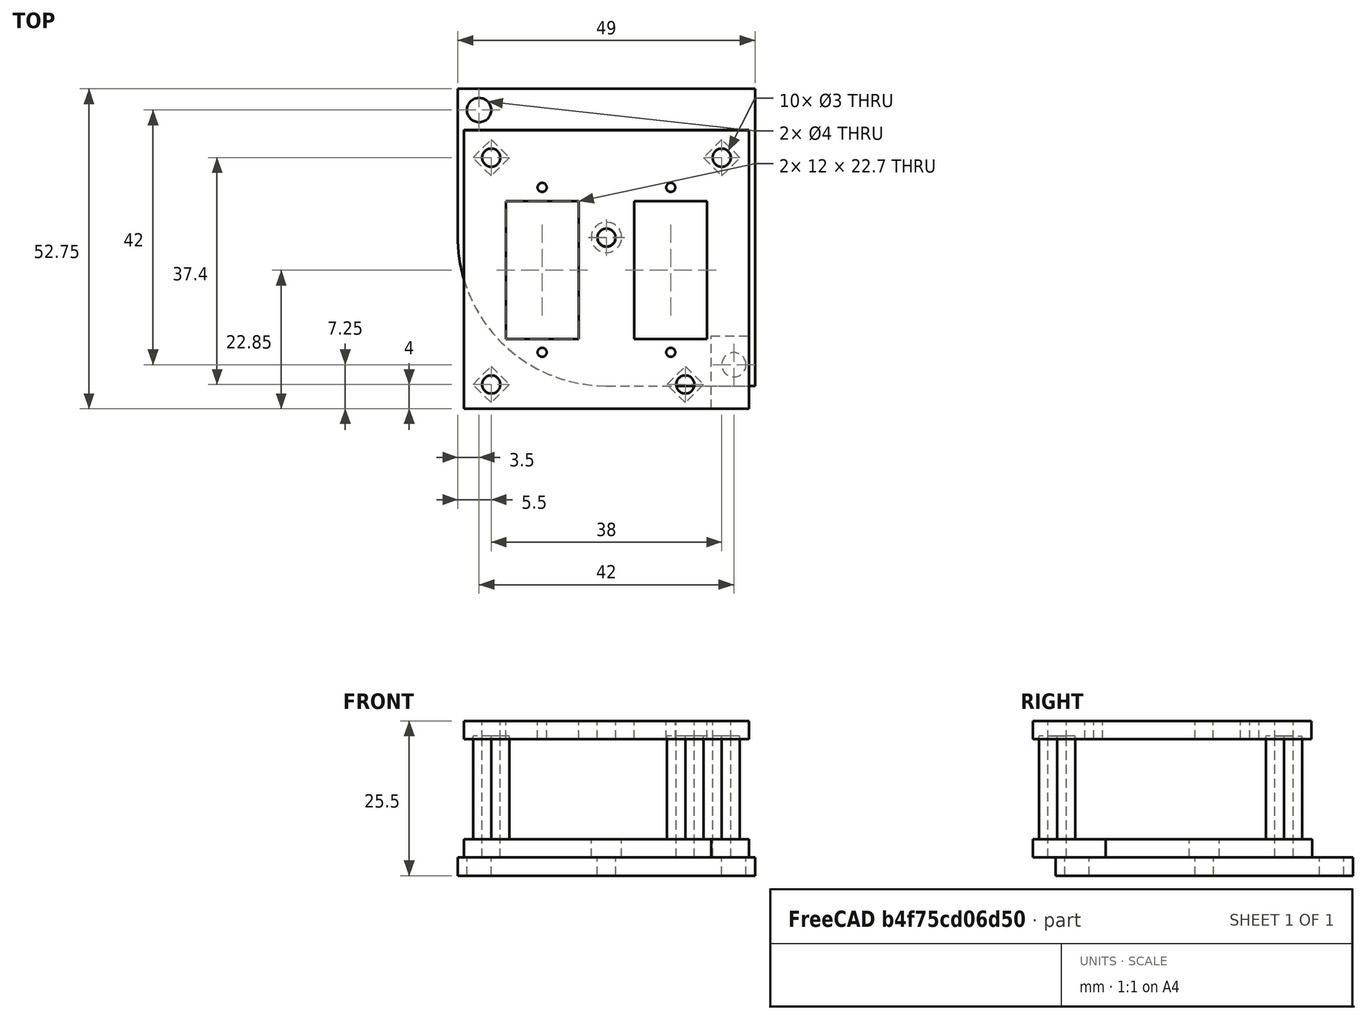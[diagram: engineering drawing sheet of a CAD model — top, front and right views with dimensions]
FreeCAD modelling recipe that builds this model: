
FCSTD DOCUMENT  (FreeCAD 0.17R13541 (Git))
Label: Temp gauge
License: All rights reserved
LicenseURL: http://en.wikipedia.org/wiki/All_rights_reserved
objects: Part::Cylinder×14, Part::Cut×13, Part::Box×7, Part::FeaturePython×5, Part::MultiFuse×4, Part::Prism×3, Part::Fuse×2
note: 48 computed .brp shape members not serialized (recipe doc carries the construction recipe); baked Part::Feature solids carry a one-line shape summary decoded from their .brp

FEATURE [Part::Box] Box  label="Temp plate"
  AttacherType = Attacher::AttachEngine3D
  Height = 3
  Length = 49
  Width = 49
FEATURE [Part::Box] Box001  label="Recorte"
  AttacherType = Attacher::AttachEngine3D
  Height = 3
  Length = 24.5
  Width = 24.5
FEATURE [Part::Cut] Cut
  Base = -> Box
  Refine = true
  Tool = -> Box001
FEATURE [Part::Cylinder] Cylinder  label="Cilindro"
  Angle = 360
  AttacherType = Attacher::AttachEngine3D
  Height = 3
  Placement = pos=(24.5,24.5,0) rot=(0,0,1;0rad)
  Radius = 24.5
FEATURE [Part::MultiFuse] Fusion  label="Temp plate recortada"
  Refine = true
  Shapes = -> [Cut,Cylinder]
FEATURE [Part::Cylinder] Cylinder001  label="Taladro 1"
  Angle = 360
  AttacherType = Attacher::AttachEngine3D
  Height = 10
  Placement = pos=(3.5,45.5,0) rot=(0,0,1;0rad)
  Radius = 2
FEATURE [Part::Cylinder] Cylinder002  label="Taladro 2"
  Angle = 360
  AttacherType = Attacher::AttachEngine3D
  Height = 10
  Placement = pos=(45.5,3.5,0) rot=(0,0,1;0rad)
  Radius = 2
FEATURE [Part::Cylinder] Cylinder003  label="Taladro 3"
  Angle = 360
  AttacherType = Attacher::AttachEngine3D
  Height = 10
  Placement = pos=(24.5,24.5,0) rot=(0,0,1;0rad)
  Radius = 1.5
FEATURE [Part::Cut] Cut001
  Base = -> Fusion
  Refine = true
  Tool = -> Cylinder001
FEATURE [Part::Cut] Cut002
  Base = -> Cut001
  Refine = true
  Tool = -> Cylinder002
FEATURE [Part::Cut] Cut003  label="temp plate final"
  Base = -> Cut002
  Refine = true
  Tool = -> Cylinder003
FEATURE [Part::Box] Box002  label="top plate 2"
  AttacherType = Attacher::AttachEngine3D
  Height = 3
  Length = 47
  Placement = pos=(3.25,-1.5,3) rot=(0,0,1;0rad)
  Width = 46
FEATURE [Part::Cylinder] Cylinder004  label="taladro 3"
  Angle = 360
  AttacherType = Attacher::AttachEngine3D
  Height = 10
  Placement = pos=(26.75,26.75,0) rot=(0,0,1;0rad)
  Radius = 2.5
FEATURE [Part::Cylinder] Cylinder005  label="taladro 4"
  Angle = 360
  AttacherType = Attacher::AttachEngine3D
  Height = 27
  Placement = pos=(7.75,2.5,0) rot=(0,0,1;0rad)
  Radius = 1.5
FEATURE [Part::Box] Box003  label="base 2"
  AttacherType = Attacher::AttachEngine3D
  Height = 3
  Length = 47
  Placement = pos=(3.25,-1.5,22.5) rot=(0,0,1;0rad)
  Width = 45.9
FEATURE [Part::Box] Box004  label="Taladro servomotor"
  AttacherType = Attacher::AttachEngine3D
  Height = 10
  Length = 12
  Placement = pos=(10.15,10,19.5) rot=(0,0,1;0rad)
  Width = 22.7
FEATURE [Part::Cylinder] Cylinder006  label="taladro 5"
  Angle = 360
  AttacherType = Attacher::AttachEngine3D
  Height = 10
  Placement = pos=(7.75,2.5,19.5) rot=(0,0,1;0rad)
  Radius = 1.5
FEATURE [Part::Cylinder] Cylinder007  label="Taladro 6"
  Angle = 360
  AttacherType = Attacher::AttachEngine3D
  Height = 10
  Placement = pos=(26.75,26.7,19.5) rot=(0,0,1;0rad)
  Radius = 1.5
FEATURE [Part::Cylinder] Cylinder008  label="Taladro 7"
  Angle = 360
  AttacherType = Attacher::AttachEngine3D
  Height = 10
  Placement = pos=(16.15,7.8,19.5) rot=(0,0,1;0rad)
  Radius = 0.75
FEATURE [Part::Cylinder] Cylinder009  label="taladro adicional 3"
  Angle = 360
  AttacherType = Attacher::AttachEngine3D
  Height = 27
  Placement = pos=(45.75,39.9,0) rot=(0,0,1;0rad)
  Radius = 1.5
FEATURE [Part::Box] Box005  label="Recorte placa"
  AttacherType = Attacher::AttachEngine3D
  Height = 3
  Length = 10
  Placement = pos=(44,-2,3) rot=(0,0,1;0rad)
  Width = 11
FEATURE [Part::FeaturePython] Array002  label="Array taladro 4"  # Draft array (typed FeaturePython)
  Angle = 360
  ArrayType = 0
  Axis = (0,0,1)
  Base = -> Cylinder005
  Center = (0,0,0)
  Fuse = false
  IntervalAxis = (0,0,0)
  IntervalX = (38,0,0)
  IntervalY = (0,37.4,0)
  IntervalZ = (0,0,0)
  NumberPolar = 1
  NumberX = 1
  NumberY = 2
  NumberZ = 1
FEATURE [Part::Fuse] Fusion002  label="Taladros 2"
  Base = -> Cylinder004
  Refine = true
  Tool = -> Array002
FEATURE [Part::Prism] Prism  label="Columna"
  AttacherType = Attacher::AttachEngine3D
  Circumradius = 3
  Height = 20
  Placement = pos=(7.75,2.5,3) rot=(0,0,1;0rad)
  Polygon = 4
FEATURE [Part::FeaturePython] Array003  label="Array columnas"  # Draft array (typed FeaturePython)
  Angle = 360
  ArrayType = 0
  Axis = (0,0,1)
  Base = -> Prism
  Center = (0,0,0)
  Fuse = false
  IntervalAxis = (0,0,0)
  IntervalX = (38,0,0)
  IntervalY = (0,37.4,0)
  IntervalZ = (0,0,0)
  NumberPolar = 1
  NumberX = 1
  NumberY = 2
  NumberZ = 1
FEATURE [Part::Fuse] Fusion001  label="top plate columnas"
  Base = -> Box002
  Refine = true
  Tool = -> Array003
FEATURE [Part::Cut] Cut004  label="Top plate"
  Base = -> Fusion001
  Refine = true
  Tool = -> Fusion002
FEATURE [Part::Prism] Prism001  label="Columna 3"
  AttacherType = Attacher::AttachEngine3D
  Circumradius = 3
  Height = 20
  Placement = pos=(45.75,39.9,3) rot=(0,0,1;0rad)
  Polygon = 4
FEATURE [Part::MultiFuse] Fusion004  label="placa con tres taladros"
  Refine = true
  Shapes = -> [Cut004,Prism001]
FEATURE [Part::Prism] Prism002  label="Columna 4"
  AttacherType = Attacher::AttachEngine3D
  Circumradius = 3
  Height = 20
  Placement = pos=(39.75,2.5,3) rot=(0,0,1;0rad)
  Polygon = 4
FEATURE [Part::FeaturePython] Array004  label="Array taladro servomotor"  # Draft array (typed FeaturePython)
  Angle = 360
  ArrayType = 0
  Axis = (0,0,1)
  Base = -> Box004
  Center = (0,0,0)
  Fuse = false
  IntervalAxis = (0,0,0)
  IntervalX = (21.2,0,0)
  IntervalY = (0,1,0)
  IntervalZ = (0,0,0)
  NumberPolar = 1
  NumberX = 2
  NumberY = 1
  NumberZ = 1
FEATURE [Part::FeaturePython] Array005  label="Array taladro 5"  # Draft array (typed FeaturePython)
  Angle = 360
  ArrayType = 0
  Axis = (0,0,1)
  Base = -> Cylinder006
  Center = (0,0,0)
  Fuse = false
  IntervalAxis = (0,0,0)
  IntervalX = (38,0,0)
  IntervalY = (0,37.4,0)
  IntervalZ = (0,0,0)
  NumberPolar = 1
  NumberX = 1
  NumberY = 2
  NumberZ = 1
FEATURE [Part::FeaturePython] Array006  label="Array taladros 7"  # Draft array (typed FeaturePython)
  Angle = 360
  ArrayType = 0
  Axis = (0,0,1)
  Base = -> Cylinder008
  Center = (0,0,0)
  Fuse = false
  IntervalAxis = (0,0,0)
  IntervalX = (21.2,0,0)
  IntervalY = (0,27.2,0)
  IntervalZ = (0,0,0)
  NumberPolar = 1
  NumberX = 2
  NumberY = 2
  NumberZ = 1
FEATURE [Part::MultiFuse] Fusion003  label="Taladros 3"
  Refine = true
  Shapes = -> [Cylinder007,Array006,Array004,Array005]
FEATURE [Part::Cut] Cut005  label="base previa"
  Base = -> Box003
  Refine = true
  Tool = -> Fusion003
FEATURE [Part::Cut] Cut006  label="Placa con tres columnas"
  Base = -> Fusion004
  Refine = true
  Tool = -> Cylinder009
FEATURE [Part::Cut] Cut007  label="Placa tres columnas y tornillo"
  Base = -> Cut006
  Refine = true
  Tool = -> Box005
FEATURE [Part::Cylinder] Cylinder010  label="taladro adicional 4"
  Angle = 360
  AttacherType = Attacher::AttachEngine3D
  Height = 27
  Placement = pos=(39.75,2.5,0) rot=(0,0,1;0rad)
  Radius = 1.5
FEATURE [Part::Cut] Cut008
  Base = -> Cut007
  Refine = true
  Tool = -> Cylinder010
FEATURE [Part::Cylinder] Cylinder011  label="taladro adicional 005"
  Angle = 360
  AttacherType = Attacher::AttachEngine3D
  Height = 27
  Placement = pos=(39.75,2.5,0) rot=(0,0,1;0rad)
  Radius = 1.5
FEATURE [Part::Cut] Cut009
  Base = -> Prism002
  Refine = true
  Tool = -> Cylinder011
FEATURE [Part::MultiFuse] Fusion005  label="top plate final"
  Placement = pos=(-2.25,-2.25,0) rot=(0,0,1;0rad)
  Refine = true
  Shapes = -> [Cut008,Cut009]
FEATURE [Part::Cylinder] Cylinder012  label="taladro 006"
  Angle = 360
  AttacherType = Attacher::AttachEngine3D
  Height = 10
  Placement = pos=(45.75,39.9,19.5) rot=(0,0,1;0rad)
  Radius = 1.5
FEATURE [Part::Cut] Cut010  label="base 3 taladros"
  Base = -> Cut005
  Refine = true
  Tool = -> Cylinder012
FEATURE [Part::Cylinder] Cylinder013  label="taladro 007"
  Angle = 360
  AttacherType = Attacher::AttachEngine3D
  Height = 10
  Placement = pos=(39.75,2.5,18.5) rot=(0,0,1;0rad)
  Radius = 1.5
FEATURE [Part::Cut] Cut011  label="base final"
  Base = -> Cut010
  Placement = pos=(-2.25,-2.25,0) rot=(0,0,1;0rad)
  Refine = true
  Tool = -> Cylinder013
FEATURE [Part::Box] Box006  label="Recorte adicional"
  AttacherType = Attacher::AttachEngine3D
  Height = 3
  Length = 7.25
  Placement = pos=(41.75,0,3) rot=(0,0,1;0rad)
  Width = 8.25
FEATURE [Part::Cut] Cut012  label="top plate final 2"
  Base = -> Fusion005
  Refine = true
  Tool = -> Box006
